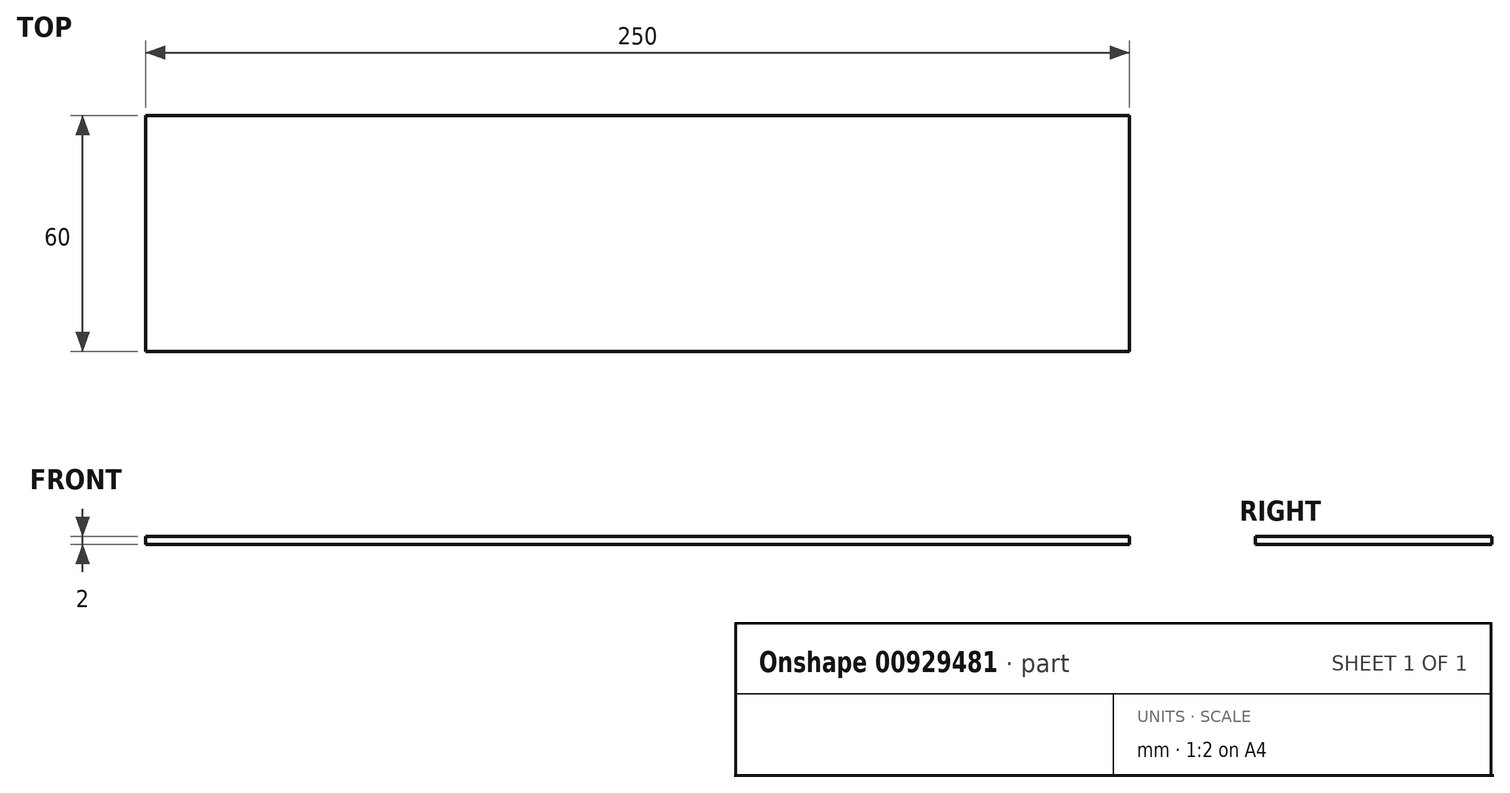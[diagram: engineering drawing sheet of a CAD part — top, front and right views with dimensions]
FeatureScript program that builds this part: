
annotation { "Feature Type Name" : "Feature", "Feature Type Description" : "" }
export const myFeature = defineFeature(function(context is Context, id is Id, definition is map)
    precondition{}
    {
        {
            var Q0;
            Q0=qCreatedBy(makeId("Top.planeOp"),FACE);
            var sketch = newSketch(context, id + "F0", { "sketchPlane" : qUnion([Q0])});
            skLineSegment(sketch, "E0.bottom", {"start": v(125, -30) * mm, "end": v(-125, -30) * mm});
            skLineSegment(sketch, "E0.top", {"start": v(125, 30) * mm, "end": v(-125, 30) * mm});
            skLineSegment(sketch, "E0.left", {"start": v(125, -30) * mm, "end": v(125, 30) * mm});
            skLineSegment(sketch, "E0.right", {"start": v(-125, -30) * mm, "end": v(-125, 30) * mm});
            skPoint(sketch, "E0.middle", {"position": v(0, 0) * mm});
            skSolve(sketch);
        }
        {
            var Q0;
            Q0 = qSketchRegion(id + "F0", true);
            extrude(context, id + "F1", {"entities" : qUnion([Q0]), "depth" : 2 * mm, "offsetDistance" : 25 * mm});
        }
    });
